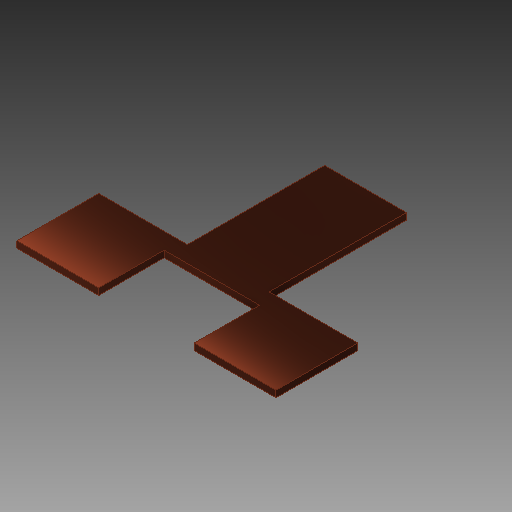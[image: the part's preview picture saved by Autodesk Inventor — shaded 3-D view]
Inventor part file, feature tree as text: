
AUTODESK INVENTOR PART (.ipt)
format: ipt  version: 2019.2 (Build 232265000, 265)  size: 100,864 bytes
history: native  units: mm
features: other x1, extrude x1, sketch x1
ambient origin geometry x8: Origin, YZ Plane, XZ Plane, XY Plane, X Axis, Y Axis, Z Axis, Center Point
bodies: Solid1 (feature_tree)
feature tree (3):
  other  "Housing Box 1.ipt"
  extrude  "Extrusion1"  Depth=2.0mm TaperAngle=0.0deg
  sketch  "Sketch19"  dims[d0=10.0mm d1=2.0mm d2=0.0mm]
